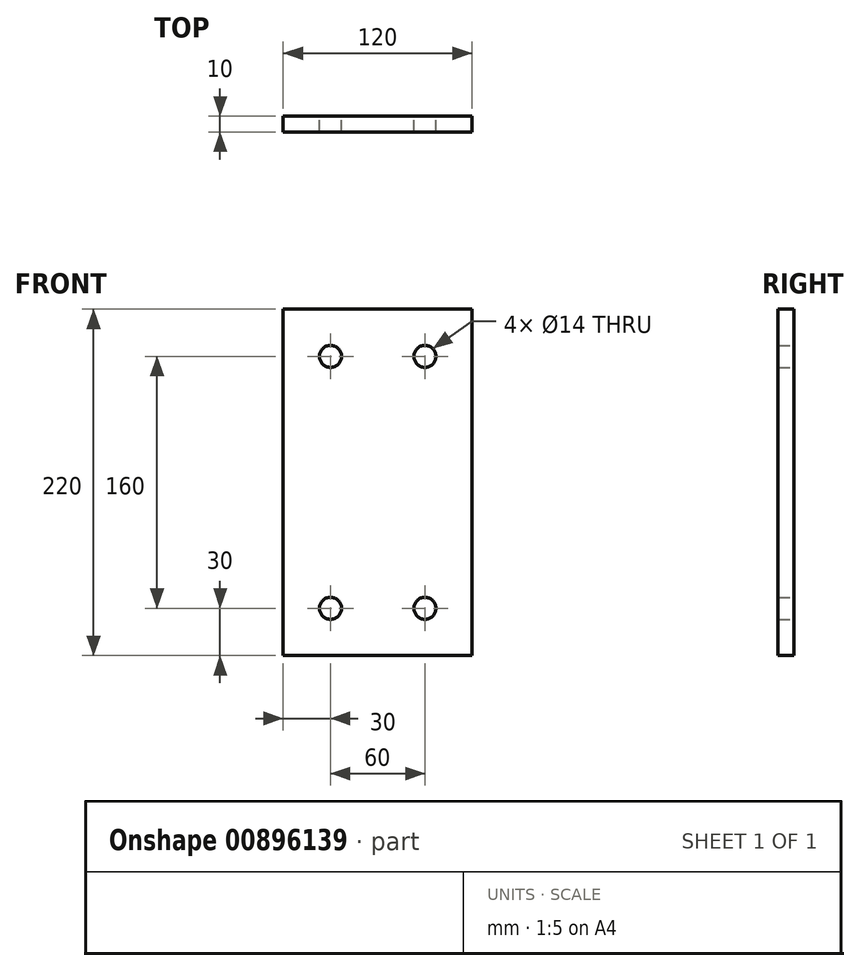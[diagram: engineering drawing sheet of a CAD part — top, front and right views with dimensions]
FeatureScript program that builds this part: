
annotation { "Feature Type Name" : "Feature", "Feature Type Description" : "" }
export const myFeature = defineFeature(function(context is Context, id is Id, definition is map)
    precondition{}
    {
        {
            var Q0;
            Q0=qCreatedBy(makeId("Front.planeOp"),FACE);
            var sketch = newSketch(context, id + "F0", { "sketchPlane" : qUnion([Q0])});
            skLineSegment(sketch, "E0.bottom", {"start": v(60, 110) * mm, "end": v(-60, 110) * mm});
            skLineSegment(sketch, "E0.top", {"start": v(60, -110) * mm, "end": v(-60, -110) * mm});
            skLineSegment(sketch, "E0.left", {"start": v(60, 110) * mm, "end": v(60, -110) * mm});
            skLineSegment(sketch, "E0.right", {"start": v(-60, 110) * mm, "end": v(-60, -110) * mm});
            skPoint(sketch, "E0.middle", {"position": v(0, 0) * mm});
            skCircle(sketch, "E1", {"center": v(-30, 80) * mm, "radius": 7 * mm});
            skCircle(sketch, "E2", {"center": v(30, 80) * mm, "radius": 7 * mm});
            skCircle(sketch, "E3", {"center": v(-30, -80) * mm, "radius": 7 * mm});
            skCircle(sketch, "E4", {"center": v(30, -80) * mm, "radius": 7 * mm});
            skSolve(sketch);
        }
        {
            var Q0;
            Q0=makeQuery(id+"F0.imprint","IMPRINT",FACE,{"disambiguationData":[TD([[makeQuery(id+"F0.imprint","IMPRINT",EDGE,{"derivedFrom":sQuery(id+"F0.wireOp",EDGE,"E0.bottom")}),1.0]])]});
            var Q1;
            Q1=makeQuery(id+"F0.imprint","IMPRINT",FACE,{"disambiguationData":[TD([[makeQuery(id+"F0.imprint","IMPRINT",EDGE,{"derivedFrom":sQuery(id+"F0.wireOp",EDGE,"IxA8HR9I-vB6L-gbE1-t8Bs-stX18FFaMMz4.bottom")}),1.0]])]});
            extrude(context, id + "F1", {"entities" : qUnion([Q0, Q1]), "depth" : 10 * mm, "offsetDistance" : 25 * mm});
        }
    });
